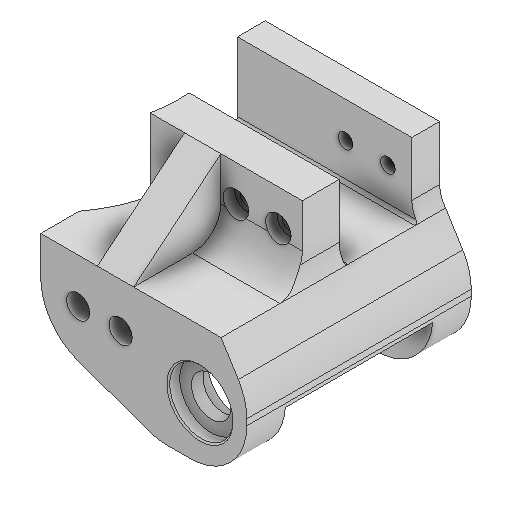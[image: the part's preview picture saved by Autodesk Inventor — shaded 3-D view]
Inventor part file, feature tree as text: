
AUTODESK INVENTOR PART (.ipt)
format: ipt  version: 2025 (Build 290162000, 162)  size: 679,424 bytes
history: native  units: in
note: dims shown in document units (in); Inventor stores cm internally (conversion verified against a paired STEP export)
features: sketch x31, extrude x30, projected_geometry x26, fillet x13, mirror x3, reference x3, other x3, chamfer x2, thicken_offset x1, plane x1, pattern_linear x1
ambient origin geometry x8: Origin, YZ Plane, XZ Plane, XY Plane, X Axis, Y Axis, Z Axis, Center Point
bodies: Solid1 (feature_tree)
feature tree (114):
  extrude  "Extrusion1"  Depth=0.25in
  extrude  "Extrusion2"  Depth=0.5512in
  extrude  "Extrusion7"  Depth=0.8809in
  extrude  "Extrusion10"  Depth=0.2165in TaperAngle=0.0deg
  extrude  "Extrusion11"  Depth=0.315in
  extrude  "Extrusion12"  TaperAngle=0.0deg  [1 undecoded]
  extrude  "Extrusion13"  Depth=0.3937in TaperAngle=0.0deg
  mirror  "Mirror1"
  fillet  "Fillet5"  Radius=0.3937in
  extrude  "Extrusion14"  Depth=0.3937in
  fillet  "Fillet6"  [1 undecoded]
  extrude  "Extrusion15"  Depth=0.3937in
  thicken_offset  "Thicken1"
  fillet  "Fillet7"  Radius=0.3858in
  extrude  "Extrusion16"  Depth=0.5118in
  extrude  "Extrusion17"  Depth=0.1969in
  fillet  "Fillet8"  Radius=1.0in
  extrude  "Extrusion18"  Depth=0.3937in
  extrude  "Extrusion19"  Depth=1.0in TaperAngle=0.0deg
  extrude  "Extrusion20"  Depth=0.315in
  extrude  "Extrusion21"  Depth=0.3228in
  extrude  "Extrusion22"  Depth=0.2756in
  extrude  "Extrusion23"  Depth=0.2047in
  plane  "Work Plane1"
  mirror  "Mirror2"
  fillet  "Fillet9"  Radius=0.2047in
  fillet  "Fillet10"  [1 undecoded]
  extrude  "Extrusion24"  Depth=0.3543in
  extrude  "Extrusion25"  Depth=0.7874in
  fillet  "Fillet12"  Radius=0.1969in
  fillet  "Fillet13"  Radius=0.1969in
  chamfer  "Chamfer1"  [1 undecoded]
  chamfer  "Chamfer2"  Distance=0.0197in Angle=45.0deg
  extrude  "Extrusion26"  Depth=0.3937in TaperAngle=0.0deg
  sketch  "Sketch27"  dims[d93=0.5in d94=0.0197in d95=0.0787in d96=45.0deg]
  extrude  "Extrusion27"  Depth=0.3937in TaperAngle=0.0deg
  extrude  "Extrusion28"  Depth=0.7874in
  extrude  "Extrusion29"  Depth=0.3937in TaperAngle=0.0deg
  pattern_linear  "Rectangular Pattern1"  Count1=2  [1 undecoded]
  extrude  "Extrusion30"  Depth=0.3937in
  extrude  "Extrusion31"  Depth=0.3937in
  extrude  "Extrusion32"  Depth=0.3937in
  fillet  "Fillet14"  Radius=0.0344in
  extrude  "Extrusion33"  TaperAngle=0.0deg  [1 undecoded]
  extrude  "Extrusion34"  TaperAngle=0.0deg  [1 undecoded]
  extrude  "Extrusion35"  TaperAngle=0.0deg  [1 undecoded]
  fillet  "Fillet15"  [1 undecoded]
  extrude  "Extrusion36"  TaperAngle=0.0deg  [1 undecoded]
  fillet  "Fillet16"  [1 undecoded]
  fillet  "Fillet18"  [1 undecoded]
  fillet  "Fillet19"  [1 undecoded]
  mirror  "Mirror3"
  sketch  "Sketch1"  dims[d1=1.005in d2=0.25in]
  sketch  "Sketch2"  dims[d3=2.0in d4=0.0in d5=0.5512in]
  projected_geometry  "Projected Loop1"
  sketch  "Sketch7"  dims[d6=0.0in d7=0.0in d21=0.8809in]
  sketch  "Sketch10"  dims[d22=0.1575in d23=0.0in d32=0.2165in d33=0.0in]
  projected_geometry  "Projected Loop7"
  sketch  "Sketch11"  dims[d34=1.1024in d35=0.315in]
  sketch  "Sketch12"  dims[d36=0.2047in d37=0.0in d38=0.0in]
  projected_geometry  "Projected Loop8"
  sketch  "Sketch13"  dims[d39=0.3937in d40=0.0in d42=1.0236in d43=0.0in d45=0.3937in]
  projected_geometry  "Projected Loop9"
  sketch  "Sketch14"  dims[d46=1.0236in d47=0.0in d48=0.3937in d49=0.0in d50=0.0in]
  projected_geometry  "Projected Loop10"
  sketch  "Sketch15"  dims[d51=0.0591in d52=0.1in d53=0.3937in d54=0.3858in]
  projected_geometry  "Projected Loop11"
  sketch  "Sketch16"  dims[d55=0.0079in d56=0.5118in]
  projected_geometry  "Projected Loop12"
  reference  "Reference1"
  sketch  "Sketch17"  dims[d57=0.2756in d58=0.1969in d59=1.0in d60=0.0in]
  projected_geometry  "Projected Loop13"
  sketch  "Sketch18"  dims[d61=1.0in d62=0.0in d63=0.3937in]
  projected_geometry  "Projected Loop14"
  reference  "Reference2"
  sketch  "Sketch19"  dims[d64=0.2047in d65=1.0in d66=0.0in]
  sketch  "Sketch20"  dims[d67=0.315in d68=0.315in]
  sketch  "Sketch21"  dims[d69=0.1969in d70=0.0in d71=0.3228in]
  sketch  "Sketch22"  dims[d72=0.315in d73=0.0in d74=0.2756in]
  reference  "Reference3"
  sketch  "Sketch23"  dims[d75=0.4724in d76=0.0in d77=0.2047in d78=0.2047in d79=0.0in d80=0.0in]
  projected_geometry  "Projected Loop15"
  sketch  "Sketch24"  dims[d81=0.3543in d82=0.3543in]
  projected_geometry  "Projected Loop16"
  projected_geometry  "Projected Loop17"
  sketch  "Sketch25"  dims[d83=0.315in d84=0.0in d85=0.7874in d86=0.1969in d88=0.1969in d89=0.0in d90=0.0in d91=0.0in]
  projected_geometry  "Projected Loop18"
  sketch  "Sketch26"  dims[d92=0.5in]
  projected_geometry  "Projected Loop19"
  sketch  "Sketch28"  dims[d97=0.1181in d98=0.0787in d99=45.0deg d100=0.3937in d101=0.0in]
  projected_geometry  "Projected Loop20"
  projected_geometry  "Projected Loop21"
  sketch  "Sketch29"  dims[d102=0.3937in d103=0.0in d104=0.3937in d105=0.0in]
  projected_geometry  "Projected Loop22"
  sketch  "Sketch30"  dims[d106=0.7874in d107=0.0in d108=0.7874in d110=0.5906in]
  projected_geometry  "Projected Loop23"
  sketch  "Sketch31"  dims[d111=0.0in d112=0.0in d113=0.3937in d114=0.0in]
  sketch  "Sketch32"  dims[d115=0.3937in d116=0.0in]
  projected_geometry  "Projected Loop24"
  sketch  "Sketch33"  dims[d117=0.0394in]
  projected_geometry  "Projected Loop25"
  projected_geometry  "Projected Loop26"
  projected_geometry  "Projected Loop27"
  sketch  "Sketch34"  dims[d118=0.3937in d119=0.0in]
  projected_geometry  "Projected Loop28"
  sketch  "Sketch35"  dims[d120=0.3937in d121=0.0in]
  projected_geometry  "Projected Loop29"
  sketch  "Sketch36"  dims[d122=0.0in d123=0.0in d124=0.7874in]
  projected_geometry  "Projected Loop30"
  sketch  "Sketch37"  dims[d125=0.2362in d126=0.0in d127=0.1969in d129=0.3937in d130=0.3937in d24=0.0344in d27=0.0in d28=0.0in d29=0.0in d30=0.0in d87=0.0in d131=0.0in d132=0.0in d133=0.0in d134=0.0in]
  projected_geometry  "Projected Loop31"
  other  "<userpath>\Desktop\puppycat\singleSwingarmV2.iam"
  other  "singleSwingarmV2.iam"
  other  "trackBase:1"
note: 13 required parameter values undecoded (feature->parameter linkage not recoverable at this tier; creation-order binding heuristic only, values carry confidence <= 0.55)
